# Revit family: Toilet_Seat-Elongated_Open_Front-KOHLER-Lustra-K-4650
name_source: partatom
category: Generic Models
revit_build: Autodesk Revit 2015 (Build: 20140606_1530(x64)
units: mm (PartAtom-declared; Revit-internal decimal feet)

## types (10) — shared parameters
ADA = No
Assembly Code = C1030200
Date Modified = 11/20/2017
Default Elevation = 0"
Height = 2 1/16"
Length = 19"
Manufacturer = KOHLER Co.
MasterFormat 1995 = 10820
MasterFormat 2004 = 10.28.13
Material = Solid Polypropylene Plastic
Product Documentation Link = http://www.us.kohler.com
Product Name = Lustra
Product Page URL = http://www.us.kohler.com
URL = https://www.us.kohler.com
Width = 14 1/4"

## per-type parameters (varying)
| type | Description | Finish | Model | Type |
| Anti-microbial Agent, 0-White | Elongated toilet seat with Anti-microbial agent | Kohler-Plastic-0-White | K-4650-A-0 | 10 |
| 0-White | Elongated toilet seat | Kohler-Plastic-0-White | K-4650-0 | 1 |
| 96-Biscuit | Elongated toilet seat | Kohler-Plastic-96-Biscuit | K-4650-96 | 2 |
| 47-Almond | Elongated toilet seat | Kohler-Plastic-47-Almond | K-4650-47 | 3 |
| NY-Dune | Elongated toilet seat | Kohler-Plastic-NY-Dune | K-4650-NY | 4 |
| 95-Ice Grey | Elongated toilet seat | Kohler-Plastic-95-Ice_Grey | K-4650-95 | 5 |
| G9-Sandbar | Elongated toilet seat | Kohler-Plastic-G9-Sandbar | K-4650-G9 | 6 |
| 33-Mexican Sand | Elongated toilet seat | Kohler-Plastic-33-Mexican_Sand | K-4650-33 | 7 |
| 58-Thunder Grey | Elongated toilet seat | Kohler-Plastic-58-Thunder_Grey | K-4650-58 | 8 |
| 7-Black Black | Elongated toilet seat | Kohler-Plastic-7-Black_Black | K-4650-7 | 9 |

## geometry (parser evidence)
native form markers: Sweep x5
no freeform markers — native parametric forms only
